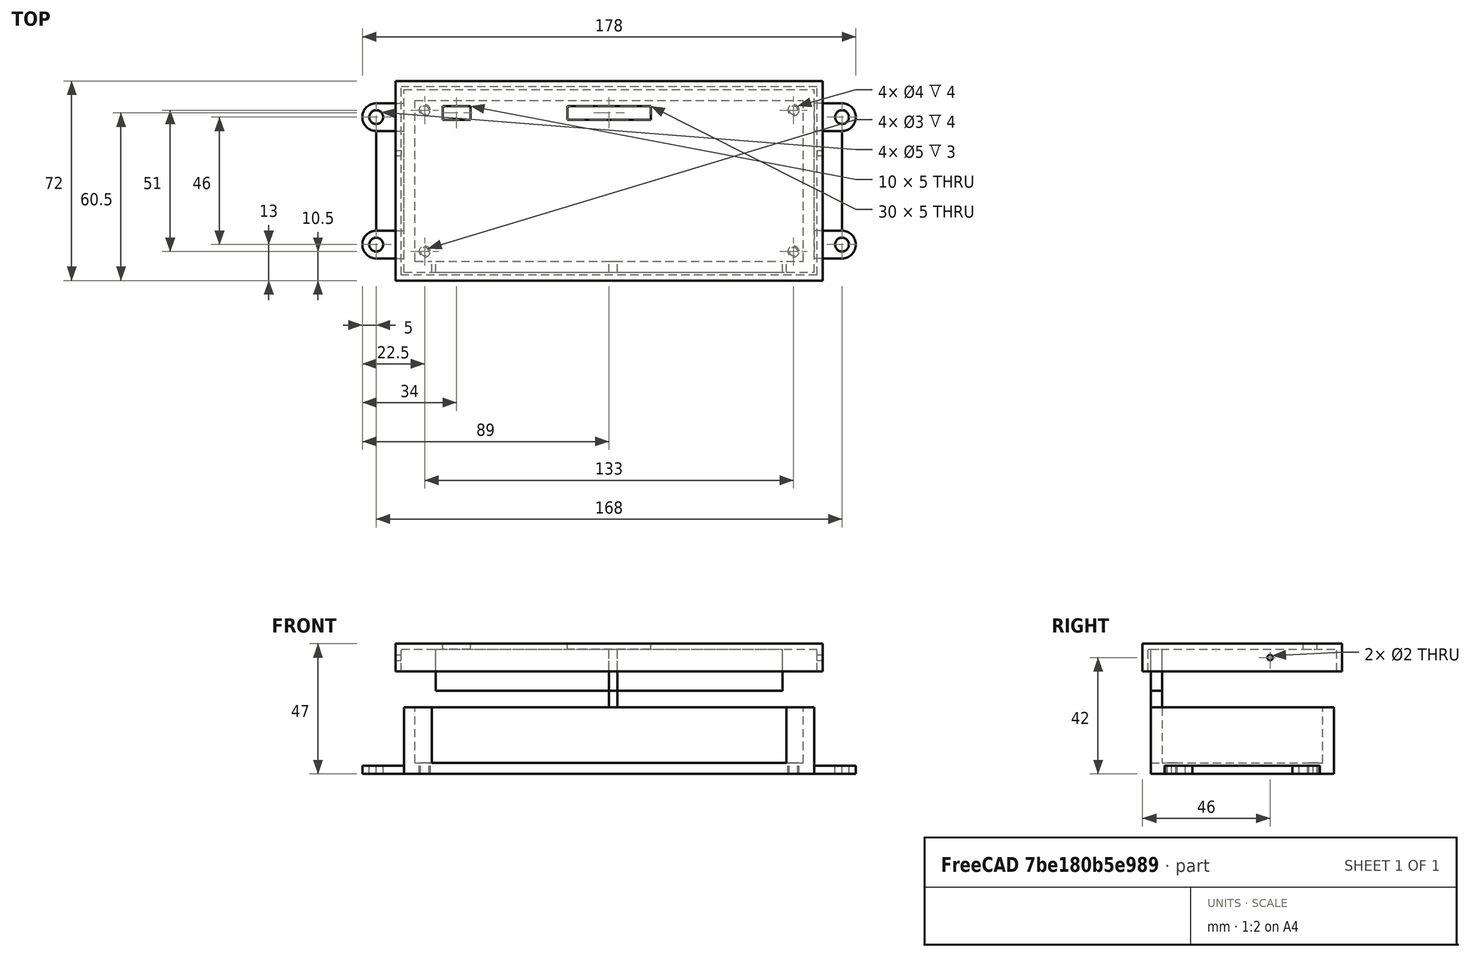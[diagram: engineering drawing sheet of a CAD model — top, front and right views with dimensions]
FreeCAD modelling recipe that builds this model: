
FCSTD DOCUMENT  (FreeCAD 0.18.4R)
Label: 8x8_relay_case
License: All rights reserved
LicenseURL: http://en.wikipedia.org/wiki/All_rights_reserved
objects: Part::Cylinder×18, Part::Box×15, Part::Cut×15, Part::Compound×5, Part::MultiFuse×4
note: 57 computed .brp shape members not serialized (recipe doc carries the construction recipe); baked Part::Feature solids carry a one-line shape summary decoded from their .brp

FEATURE [Part::Box] Box  label="Cube"
  AttacherType = Attacher::AttachEngine3D
  Height = 24
  Length = 148
  Placement = pos=(-74,-33,-4) rot=(0,0,1;0rad)
  Width = 66
FEATURE [Part::Box] Box001  label="Cube001"
  AttacherType = Attacher::AttachEngine3D
  Height = 20
  Length = 140
  Placement = pos=(-70,-29,0) rot=(0,0,1;0rad)
  Width = 58
FEATURE [Part::Cut] Cut  label="Base"
  Base = -> Box
  Tool = -> Box001
FEATURE [Part::Box] Box002  label="Cube002"
  AttacherType = Attacher::AttachEngine3D
  Height = 21
  Length = 128
  Placement = pos=(-64,-36,0) rot=(0,0,1;0rad)
  Width = 10
FEATURE [Part::Cut] Cut001
  Base = -> Cut
  Tool = -> Box002
FEATURE [Part::Cylinder] Cylinder
  Angle = 360
  AttacherType = Attacher::AttachEngine3D
  Height = 4
  Placement = pos=(-66.5,25.5,-4) rot=(0,0,1;0rad)
  Radius = 2
FEATURE [Part::Cylinder] Cylinder001
  Angle = 360
  AttacherType = Attacher::AttachEngine3D
  Height = 4
  Placement = pos=(-66.5,-25.5,-4) rot=(0,0,1;0rad)
  Radius = 2
FEATURE [Part::Cylinder] Cylinder002
  Angle = 360
  AttacherType = Attacher::AttachEngine3D
  Height = 4
  Placement = pos=(66.5,25.5,-4) rot=(0,0,1;0rad)
  Radius = 2
FEATURE [Part::Cylinder] Cylinder003
  Angle = 360
  AttacherType = Attacher::AttachEngine3D
  Height = 4
  Placement = pos=(66.5,-25.5,-4) rot=(0,0,1;0rad)
  Radius = 2
FEATURE [Part::Compound] Compound
  Links = -> [Cut001,Cylinder003,Cylinder,Cylinder002,Cylinder001]
FEATURE [Part::Cylinder] Cylinder004
  Angle = 360
  AttacherType = Attacher::AttachEngine3D
  Height = 10
  Placement = pos=(66.5,25.5,-5) rot=(0,0,1;0rad)
  Radius = 1.5
FEATURE [Part::Cylinder] Cylinder005
  Angle = 360
  AttacherType = Attacher::AttachEngine3D
  Height = 10
  Placement = pos=(-66.5,25.5,-5) rot=(0,0,1;0rad)
  Radius = 1.5
FEATURE [Part::Cylinder] Cylinder006
  Angle = 360
  AttacherType = Attacher::AttachEngine3D
  Height = 10
  Placement = pos=(66.5,-25.5,-5) rot=(0,0,1;0rad)
  Radius = 1.5
FEATURE [Part::Cylinder] Cylinder007
  Angle = 360
  AttacherType = Attacher::AttachEngine3D
  Height = 10
  Placement = pos=(-66.5,-25.5,-5) rot=(0,0,1;0rad)
  Radius = 1.5
FEATURE [Part::Cut] Cut002
  Base = -> Compound
  Tool = -> Cylinder004
FEATURE [Part::Cut] Cut003
  Base = -> Cut002
  Tool = -> Cylinder007
FEATURE [Part::Cut] Cut004
  Base = -> Cut003
  Tool = -> Cylinder006
FEATURE [Part::Cut] Cut005  label="Base001"
  Base = -> Cut004
  Tool = -> Cylinder005
FEATURE [Part::Box] Box003  label="Cube003"
  AttacherType = Attacher::AttachEngine3D
  Height = 3
  Length = 10
  Placement = pos=(-84,18,-4) rot=(0,0,1;0rad)
  Width = 10
FEATURE [Part::Cylinder] Cylinder008
  Angle = 360
  AttacherType = Attacher::AttachEngine3D
  Height = 3
  Placement = pos=(-84,23,-4) rot=(0,0,1;0rad)
  Radius = 5
FEATURE [Part::Cylinder] Cylinder009
  Angle = 360
  AttacherType = Attacher::AttachEngine3D
  Height = 10
  Placement = pos=(-84,23,-6) rot=(0,0,1;0rad)
  Radius = 2.5
FEATURE [Part::MultiFuse] Fusion
  Shapes = -> [Box003,Cylinder008]
FEATURE [Part::Cut] Cut006  label="Tab001"
  Base = -> Fusion
  Tool = -> Cylinder009
FEATURE [Part::Box] Box004  label="Cube004"
  AttacherType = Attacher::AttachEngine3D
  Height = 3
  Length = 10
  Placement = pos=(-84,18,-4) rot=(0,0,1;0rad)
  Width = 10
FEATURE [Part::Cylinder] Cylinder010
  Angle = 360
  AttacherType = Attacher::AttachEngine3D
  Height = 3
  Placement = pos=(-84,23,-4) rot=(0,0,1;0rad)
  Radius = 5
FEATURE [Part::Cylinder] Cylinder011
  Angle = 360
  AttacherType = Attacher::AttachEngine3D
  Height = 10
  Placement = pos=(-84,23,-6) rot=(0,0,1;0rad)
  Radius = 2.5
FEATURE [Part::MultiFuse] Fusion001
  Shapes = -> [Box004,Cylinder010]
FEATURE [Part::Cut] Cut007  label="Tab002"
  Base = -> Fusion001
  Placement = pos=(0,-46,0) rot=(0,0,1;0rad)
  Tool = -> Cylinder011
FEATURE [Part::Box] Box005  label="Cube005"
  AttacherType = Attacher::AttachEngine3D
  Height = 3
  Length = 10
  Placement = pos=(-84,18,-4) rot=(0,0,1;0rad)
  Width = 10
FEATURE [Part::Cylinder] Cylinder012
  Angle = 360
  AttacherType = Attacher::AttachEngine3D
  Height = 3
  Placement = pos=(-84,23,-4) rot=(0,0,1;0rad)
  Radius = 5
FEATURE [Part::Cylinder] Cylinder013
  Angle = 360
  AttacherType = Attacher::AttachEngine3D
  Height = 10
  Placement = pos=(-84,23,-6) rot=(0,0,1;0rad)
  Radius = 2.5
FEATURE [Part::MultiFuse] Fusion002
  Shapes = -> [Box005,Cylinder012]
FEATURE [Part::Cut] Cut008  label="Tab003"
  Base = -> Fusion002
  Placement = pos=(0,0,0) rot=(0,0,1;3.14159rad)
  Tool = -> Cylinder013
FEATURE [Part::Cylinder] Cylinder014
  Angle = 360
  AttacherType = Attacher::AttachEngine3D
  Height = 3
  Placement = pos=(-84,23,-4) rot=(0,0,1;0rad)
  Radius = 5
FEATURE [Part::Box] Box006  label="Cube006"
  AttacherType = Attacher::AttachEngine3D
  Height = 3
  Length = 10
  Placement = pos=(-84,18,-4) rot=(0,0,1;0rad)
  Width = 10
FEATURE [Part::MultiFuse] Fusion003
  Shapes = -> [Box006,Cylinder014]
FEATURE [Part::Cylinder] Cylinder015
  Angle = 360
  AttacherType = Attacher::AttachEngine3D
  Height = 10
  Placement = pos=(-84,23,-6) rot=(0,0,1;0rad)
  Radius = 2.5
FEATURE [Part::Cut] Cut009  label="Tab004"
  Base = -> Fusion003
  Placement = pos=(0,46,0) rot=(0,0,1;3.14159rad)
  Tool = -> Cylinder015
FEATURE [Part::Box] Box007  label="Flange001"
  AttacherType = Attacher::AttachEngine3D
  Height = 3
  Length = 10
  Placement = pos=(-84,-18,-4) rot=(0,0,1;0rad)
  Width = 36
FEATURE [Part::Box] Box008  label="Flange002"
  AttacherType = Attacher::AttachEngine3D
  Height = 3
  Length = 10
  Placement = pos=(74,-18,-4) rot=(0,0,1;0rad)
  Width = 36
FEATURE [Part::Compound] Compound001  label="8x8_relay_tray_base"
  Links = -> [Cut005,Cut009,Cut008,Cut007,Cut006,Box007,Box008]
FEATURE [Part::Box] Box009  label="Cube007"
  AttacherType = Attacher::AttachEngine3D
  Height = 10
  Length = 150
  Placement = pos=(-75,-34,31) rot=(0,0,1;0rad)
  Width = 68
FEATURE [Part::Box] Box010  label="Cube008"
  AttacherType = Attacher::AttachEngine3D
  Height = 10
  Length = 154
  Placement = pos=(-77,-36,33) rot=(0,0,1;0rad)
  Width = 72
FEATURE [Part::Cut] Cut010
  Base = -> Box010
  Tool = -> Box009
FEATURE [Part::Box] Box011  label="Cube009"
  AttacherType = Attacher::AttachEngine3D
  Height = 21
  Length = 3
  Placement = pos=(0,-33,20) rot=(0,0,1;0rad)
  Width = 4
FEATURE [Part::Compound] Compound002
  Links = -> [Box011]
FEATURE [Part::Box] Box012  label="Cube010"
  AttacherType = Attacher::AttachEngine3D
  Height = 15
  Length = 125
  Placement = pos=(-62.5,-33,26) rot=(0,0,1;0rad)
  Width = 4
FEATURE [Part::Compound] Compound003
  Links = -> [Compound002,Box012,Box011]
FEATURE [Part::Box] Box013  label="Cube011"
  AttacherType = Attacher::AttachEngine3D
  Height = 10
  Length = 30
  Placement = pos=(-15,22,36) rot=(0,0,1;0rad)
  Width = 5
FEATURE [Part::Compound] Compound004
  Links = -> [Cut010,Compound003]
FEATURE [Part::Cut] Cut011
  Base = -> Compound004
  Tool = -> Box013
FEATURE [Part::Box] Box014  label="Cube012"
  AttacherType = Attacher::AttachEngine3D
  Height = 10
  Length = 10
  Placement = pos=(-60,22,37) rot=(0,0,1;0rad)
  Width = 5
FEATURE [Part::Cut] Cut012  label="lid"
  Base = -> Cut011
  Tool = -> Box014
FEATURE [Part::Cylinder] Cylinder016
  Angle = 360
  AttacherType = Attacher::AttachEngine3D
  Height = 10
  Placement = pos=(71,10,38) rot=(0,1,0;1.5708rad)
  Radius = 1
FEATURE [Part::Cylinder] Cylinder017
  Angle = 360
  AttacherType = Attacher::AttachEngine3D
  Height = 10
  Placement = pos=(-82,10,38) rot=(0,1,0;1.5708rad)
  Radius = 1
FEATURE [Part::Cut] Cut013
  Base = -> Cut012
  Tool = -> Cylinder016
FEATURE [Part::Cut] Cut014  label="8x8_relay_tray_lid"
  Base = -> Cut013
  Tool = -> Cylinder017
